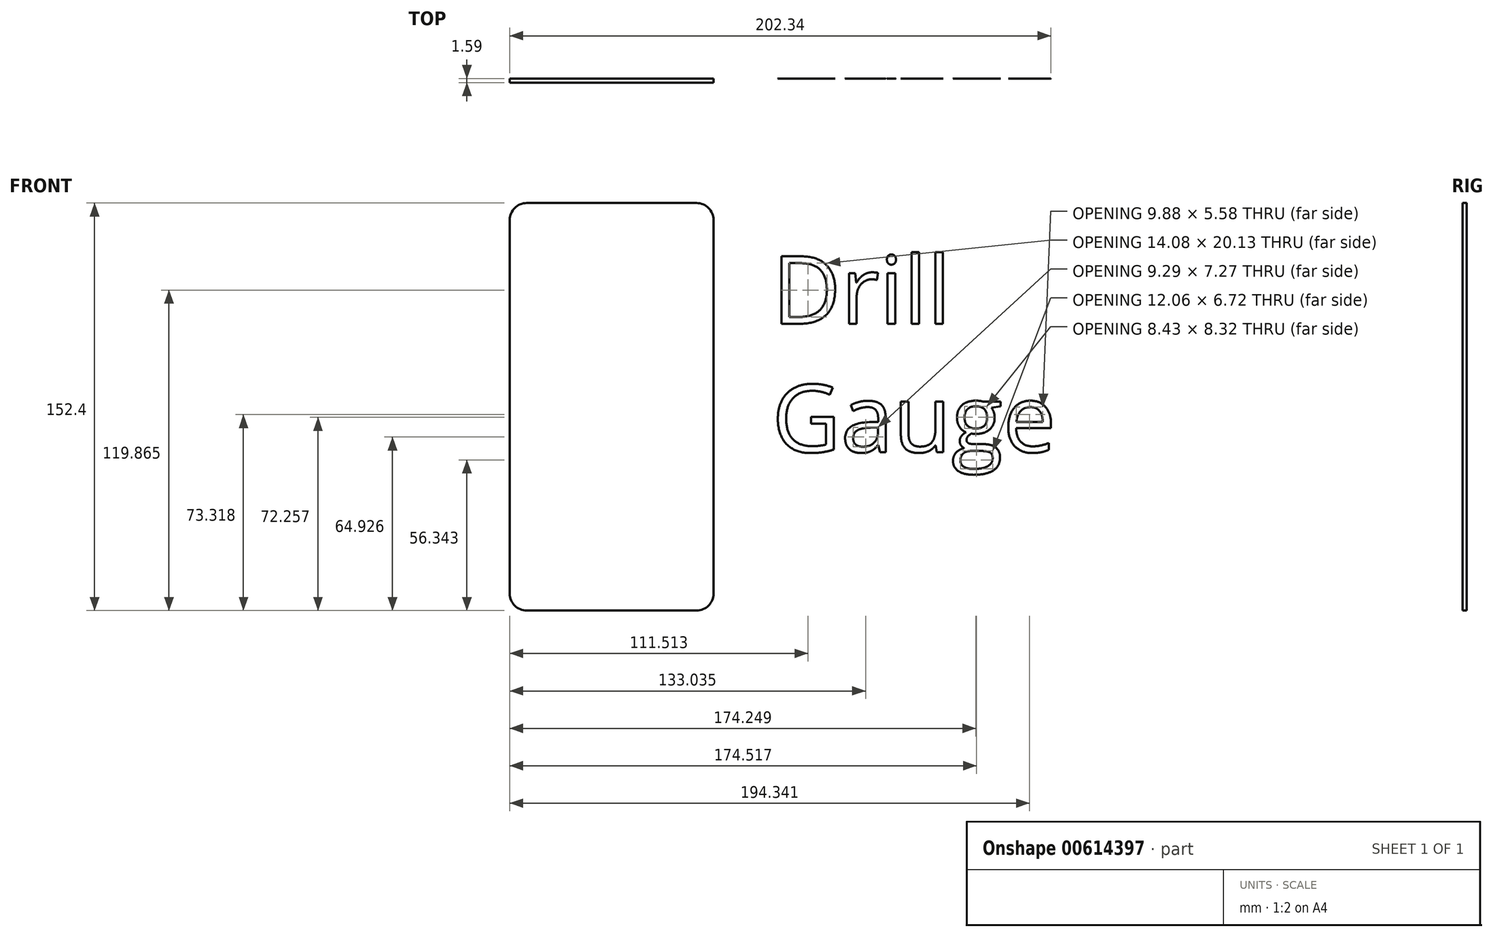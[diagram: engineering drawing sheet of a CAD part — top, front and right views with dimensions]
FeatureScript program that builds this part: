
annotation { "Feature Type Name" : "Feature", "Feature Type Description" : "" }
export const myFeature = defineFeature(function(context is Context, id is Id, definition is map)
    precondition{}
    {
        {
            var Q0;
            Q0=qCreatedBy(makeId("Front.planeOp"),FACE);
            var sketch = newSketch(context, id + "F0", { "sketchPlane" : qUnion([Q0])});
            skLineSegment(sketch, "E0.bottom", {"start": v(31.75, -76.2) * mm, "end": v(-31.75, -76.2) * mm});
            skLineSegment(sketch, "E0.top", {"start": v(31.75, 76.2) * mm, "end": v(-31.75, 76.2) * mm});
            skLineSegment(sketch, "E0.left", {"start": v(38.1, -69.85) * mm, "end": v(38.1, 69.85) * mm});
            skLineSegment(sketch, "E0.right", {"start": v(-38.1, -69.85) * mm, "end": v(-38.1, 69.85) * mm});
            skPoint(sketch, "E0.middle", {"position": v(0, 0) * mm});
            skPoint(sketch, "E1.visualSharp", {"position": v(-38.1, 76.2) * mm});
            skArc(sketch, "E1.filletArc", {"start": v(-31.75, 76.2) * mm, "mid": v(-36.24, 74.34) * mm, "end": v(-38.1, 69.85) * mm});
            skPoint(sketch, "E2.visualSharp", {"position": v(38.1, 76.2) * mm});
            skArc(sketch, "E2.filletArc", {"start": v(38.1, 69.85) * mm, "mid": v(36.24, 74.34) * mm, "end": v(31.75, 76.2) * mm});
            skPoint(sketch, "E3.visualSharp", {"position": v(38.1, -76.2) * mm});
            skArc(sketch, "E3.filletArc", {"start": v(31.75, -76.2) * mm, "mid": v(36.24, -74.34) * mm, "end": v(38.1, -69.85) * mm});
            skPoint(sketch, "E4.visualSharp", {"position": v(-38.1, -76.2) * mm});
            skArc(sketch, "E4.filletArc", {"start": v(-38.1, -69.85) * mm, "mid": v(-36.24, -74.34) * mm, "end": v(-31.75, -76.2) * mm});
            skSolve(sketch);
        }
        {
            var Q0;
            Q0=qCreatedBy(makeId("Front.planeOp"),FACE);
            var sketch = newSketch(context, id + "F1", { "sketchPlane" : qUnion([Q0])});
            skText(sketch, "E5", { "text": "Drill\nGauge", "fontName": "OpenSans-Regular.ttf"});
            const initialGuessF1  = {"E5": [0.05998, 0.03107, 1, 0, 0.02541]};
            skSetInitialGuess(sketch, initialGuessF1);
            skSolve(sketch);
        }
        {
            var Q0;
            Q0 = qSketchRegion(id + "F0", true);
            extrude(context, id + "F2", {"entities" : qUnion([Q0]), "depth" : 1.59 * mm, "offsetDistance" : 25.4 * mm});
        }
        {
            var Q0;
            Q0 = qSketchRegion(id + "F1", true);
            extrude(context, id + "F3", {"entities" : qUnion([Q0]), "depth" : ((1 / 16) / 2) * mm, "offsetDistance" : 25.4 * mm});
        }
    });
